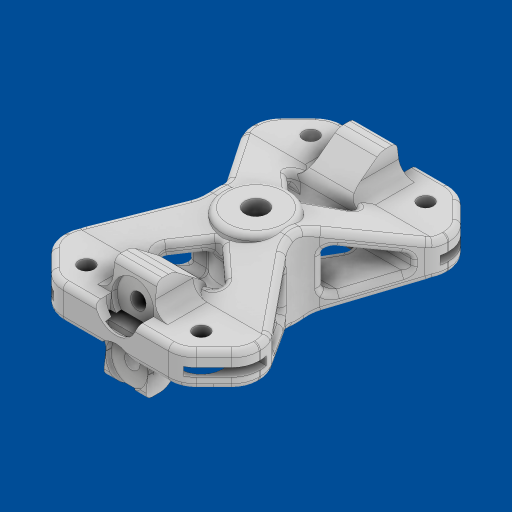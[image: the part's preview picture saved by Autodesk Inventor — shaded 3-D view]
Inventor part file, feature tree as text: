
AUTODESK INVENTOR PART (.ipt)
format: ipt  version: 2023 (Build 270158000, 158)  size: 1,703,424 bytes
history: native  units: mm
features: extrude x19, fillet x18, sketch x6, chamfer x4, mirror x3, plane x1, loft x1, other x1
ambient origin geometry x8: Origin, YZ Plane, XZ Plane, XY Plane, X Axis, Y Axis, Z Axis, Center Point
bodies: Body1 (feature_tree)
feature tree (53):
  sketch  "Sketch1"  dims[d13=261.822mm d14=7.45mm]
  plane  "Work Plane1"
  sketch  "Sketch2"  dims[d15=27.223mm d17=1.0mm]
  extrude  "Extrusion26"  Depth=7.45mm
  extrude  "Extrusion27"  Depth=1.0mm
  loft  "Loft4"
  extrude  "Extrusion30"  Depth=1.0mm
  extrude  "Extrusion32"  Depth=1.0mm
  extrude  "Extrusion33"  Depth=15.0mm
  chamfer  "Chamfer7"  Distance=65.0mm
  chamfer  "Chamfer8"  Distance=12.0mm
  fillet  "Fillet9"  Radius=1.0mm
  mirror  "Mirror1"
  extrude  "Extrusion45"  Depth=5.0mm
  extrude  "Extrusion48"  Depth=5.0mm TaperAngle=0.0deg
  extrude  "Extrusion49"  Depth=5.0mm
  sketch  "Sketch17"  dims[d23=2.0mm d25=1.0mm]
  extrude  "Extrusion51"  Depth=5.0mm
  fillet  "Fillet30"  Radius=30.0mm
  extrude  "Extrusion54"  Depth=5.0mm TaperAngle=0.0deg
  extrude  "Extrusion55"  Depth=5.0mm
  extrude  "Extrusion57"  TaperAngle=0.0deg  [1 undecoded]
  extrude  "Extrusion58"  TaperAngle=0.0deg  [1 undecoded]
  extrude  "Extrusion59"  Depth=5.0mm TaperAngle=0.0deg
  extrude  "Extrusion60"  Depth=5.0mm
  chamfer  "Chamfer15"  Distance=15.0mm
  chamfer  "Chamfer16"  Distance=15.0mm
  mirror  "Mirror3"
  extrude  "Extrusion61"  Depth=5.0mm TaperAngle=45.0deg
  extrude  "Extrusion62"  Depth=5.0mm TaperAngle=45.0deg
  extrude  "Extrusion63"  Depth=10.0mm
  fillet  "Fillet34"  Radius=15.0mm
  fillet  "Fillet35"  Radius=30.0mm
  fillet  "Fillet37"  Radius=14.0mm
  fillet  "Fillet38"  Radius=100.0mm
  extrude  "Extrusion64"  Depth=10.0mm
  mirror  "Mirror4"
  fillet  "Fillet39"  Radius=100.0mm
  fillet  "Fillet42"  Radius=15.0mm
  fillet  "Fillet43"  Radius=15.0mm
  fillet  "Fillet44"  Radius=15.0mm
  fillet  "Fillet45"  Radius=15.0mm
  fillet  "Fillet46"  Radius=7.5mm
  fillet  "Fillet47"  Radius=15.0mm
  fillet  "Fillet48"  Radius=5.5mm
  fillet  "Fillet49"  Radius=15.0mm
  fillet  "Fillet50"  Radius=2.5mm
  fillet  "Fillet51"  Radius=15.0mm
  fillet  "Fillet52"  Radius=15.0mm
  sketch  "Sketch12"  dims[d21=35.0mm d22=100.0mm]
  other  "Edges5"
  sketch  "Sketch18"  dims[d26=90.0deg d27=1.0mm]
  sketch  "Sketch19"  dims[d28=90.0deg d29=5.5mm d30=15.0mm d31=65.0mm d56=12.0mm d74=1.0mm d75=8.0mm d148=244.423mm d149=41.005864mm d150=244.423mm d151=5.5mm d152=5.5mm d153=5.5mm d154=15.0mm d155=15.0mm d156=18.0mm d157=5.5mm d158=160.0mm d159=7.0mm d160=0.0mm d161=8.0mm d162=24.0mm d163=30.0mm d164=0.0mm d165=5.0mm d166=0.0mm d167=19.96mm d170=0.0mm d171=90.0deg d172=0.0mm d173=90.0deg d178=2.0mm d179=0.0mm d180=2.0mm d183=15.0mm d184=0.0mm d185=15.0mm d186=0.0mm d206=12.0mm d207=12.0mm d208=45.0deg d209=12.0mm d210=12.0mm d211=45.0deg d212=10.0mm d256=15.0mm d257=30.0mm d258=0.0mm d271=14.0mm d272=100.0mm d273=10.0mm d274=100.0mm d276=15.0mm d277=0.0mm d287=15.0mm d288=0.0mm d289=15.0mm d290=15.0mm d291=7.5mm d292=15.0mm d293=5.5mm d296=15.0mm d297=2.5mm d298=15.0mm d299=15.0mm d300=7.5mm d301=15.0mm d302=5.5mm d303=15.0mm d304=0.0mm d310=2.0mm d311=2.0mm d312=0.0mm d313=5.0mm d316=5.0mm d317=5.0mm d318=16.0mm d319=100.0mm d320=0.0mm d324=35.0mm d325=0.0mm d326=40.0mm d327=0.0mm d328=20.0mm d329=0.0mm d330=12.0mm d331=0.0mm d333=5.0mm d334=12.0mm d335=9.168mm d336=45.0deg d337=15.0mm d338=10.835mm d339=45.0deg d341=5.0mm d342=30.0mm d343=0.0mm d344=30.0mm d345=0.0mm d346=30.0mm d347=0.0mm d348=10.0mm d349=10.0mm d351=2.0mm d352=2.0mm d353=2.0mm d354=0.0mm d355=2.0mm d358=2.0mm d359=2.0mm d360=2.0mm d361=2.0mm d362=2.0mm d363=2.0mm d364=2.0mm d365=2.0mm d366=2.0mm d367=5.0mm d368=5.0mm d369=1.0mm d370=0.0mm d76=0.5mm d77=0.872665mm d144=0.5mm d145=0.872665mm d146=0.5mm d147=0.872665mm d241=0.0mm d242=0.0mm d243=0.0mm d244=0.0mm d268=0.0mm d269=0.0mm d270=0.0mm d350=0.0mm d357=0.0mm]
note: 2 required parameter values undecoded (feature->parameter linkage not recoverable at this tier; creation-order binding heuristic only, values carry confidence <= 0.55)
